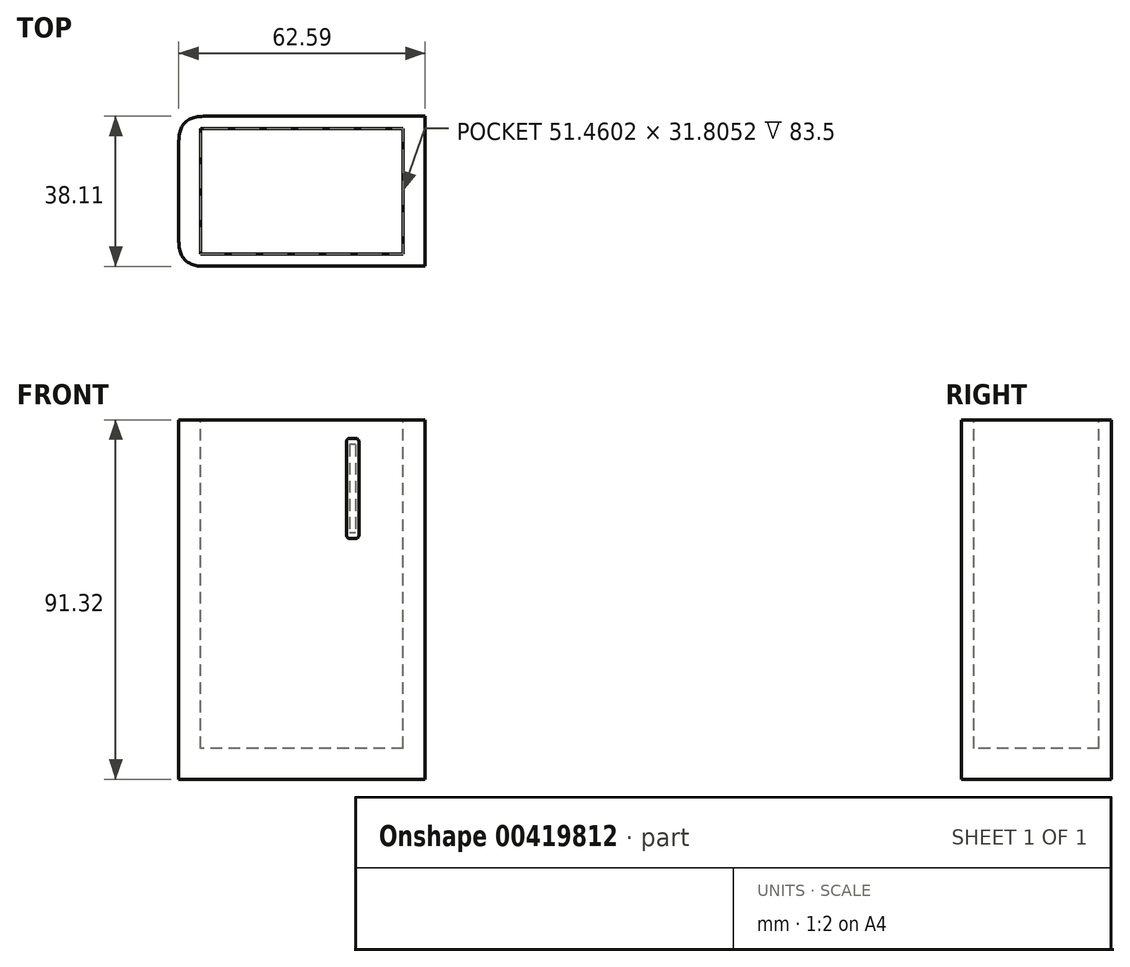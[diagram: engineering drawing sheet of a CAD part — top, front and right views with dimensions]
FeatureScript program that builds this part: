
annotation { "Feature Type Name" : "Feature", "Feature Type Description" : "" }
export const myFeature = defineFeature(function(context is Context, id is Id, definition is map)
    precondition{}
    {
        {
            var Q0;
            Q0=qCreatedBy(makeId("Front.planeOp"),FACE);
            var sketch = newSketch(context, id + "F0", { "sketchPlane" : qUnion([Q0])});
            skLineSegment(sketch, "E0", {"start": v(-32.63, 45.72) * mm, "end": v(-32.63, -30.6) * mm});
            skLineSegment(sketch, "E1", {"start": v(-32.63, -30.6) * mm, "end": v(49.96, -30.6) * mm});
            skLineSegment(sketch, "E2", {"start": v(49.96, -30.6) * mm, "end": v(49.96, 45.72) * mm});
            skLineSegment(sketch, "E3", {"start": v(49.96, 45.72) * mm, "end": v(-32.63, 45.72) * mm});
            skSolve(sketch);
        }
        {
            var Q0;
            Q0=makeQuery(id+"F0.imprint","IMPRINT",FACE,{"disambiguationData":[TD([[makeQuery(id+"F0.imprint","IMPRINT",EDGE,{"derivedFrom":sQuery(id+"F0.wireOp",EDGE,"E0")}),1.0]])]});
            extrude(context, id + "F1", {"entities" : qUnion([Q0]), "depth" : 25.4 * mm});
        }
        {
            var Q0;
            Q0=makeQuery(id+"F1.opExtrude","CAP_FACE",FACE,{"disambiguationData":[OSD([sQuery(id+"F0.wireOp",EDGE,"E0"),sQuery(id+"F0.wireOp",EDGE,"E1"),sQuery(id+"F0.wireOp",EDGE,"E2"),sQuery(id+"F0.wireOp",EDGE,"E3")])],"isStart":false});
            extrude(context, id + "F2", {"entities" : qUnion([Q0]), "operationType" : NewBodyOperationType.ADD, "depth" : 12.7 * mm});
        }
        {
            var Q0;
            {var subQ0=sQuery(id+"F0.wireOp",EDGE,"E3");Q0=makeQuery(id+"F2.boolean.opBoolean","MERGE",FACE,{"derivedFrom":[makeQuery(id+"F1.opExtrude","SWEPT_FACE",FACE,{"disambiguationData":[OSD([subQ0])]}),makeQuery(id+"F2.opExtrude","SWEPT_FACE",FACE,{"disambiguationData":[OSD([subQ0])]})]});}
            var sketch = newSketch(context, id + "F3", { "sketchPlane" : qUnion([Q0])});
            skLineSegment(sketch, "E4.bottom", {"start": v(44.4, -3.15) * mm, "end": v(-27.07, -3.15) * mm});
            skLineSegment(sketch, "E4.top", {"start": v(44.4, -34.95) * mm, "end": v(-27.07, -34.95) * mm});
            skLineSegment(sketch, "E4.left", {"start": v(44.4, -3.15) * mm, "end": v(44.4, -34.95) * mm});
            skLineSegment(sketch, "E4.right", {"start": v(-27.07, -3.15) * mm, "end": v(-27.07, -34.95) * mm});
            skPoint(sketch, "E4.middle", {"position": v(8.66, -19.05) * mm});
            skPoint(sketch, "E4.middle.positionSnap0", {"position": v(-32.63, -19.05) * mm});
            skPoint(sketch, "E4.middle.positionSnap1", {"position": v(8.66, 0) * mm});
            skPoint(sketch, "E4.centerSnap0", {"position": v(-32.63, -19.05) * mm});
            skPoint(sketch, "E4.centerSnap1", {"position": v(8.66, 0) * mm});
            skSolve(sketch);
        }
        {
            var Q0;
            Q0=makeQuery(id+"F3.imprint","IMPRINT",FACE,{"disambiguationData":[TD([[makeQuery(id+"F3.imprint","IMPRINT",EDGE,{"derivedFrom":sQuery(id+"F3.wireOp",EDGE,"E4.bottom")}),1.0]])]});
            extrude(context, id + "F4", {"entities" : qUnion([Q0]), "operationType" : NewBodyOperationType.REMOVE, "oppositeDirection" : true, "depth" : 63.5 * mm});
        }
        {
            var Q0;
            Q0=makeQuery(id+"F2.opExtrude","CAP_FACE",FACE,{"disambiguationData":[OSD([sQuery(id+"F0.wireOp",EDGE,"E0"),sQuery(id+"F0.wireOp",EDGE,"E1"),sQuery(id+"F0.wireOp",EDGE,"E2"),sQuery(id+"F0.wireOp",EDGE,"E3")])],"isStart":false});
            var sketch = newSketch(context, id + "F5", { "sketchPlane" : qUnion([Q0])});
            skLineSegment(sketch, "E5", {"start": v(49.96, 45.72) * mm, "end": v(12.33, 45.72) * mm});
            skLineSegment(sketch, "E6", {"start": v(49.96, 45.72) * mm, "end": v(49.96, 39.4) * mm});
            skLineSegment(sketch, "E7", {"start": v(12.33, 39.4) * mm, "end": v(10.8, 39.4) * mm});
            skLineSegment(sketch, "E8", {"start": v(10.8, 39.4) * mm, "end": v(10.8, 17.15) * mm});
            skLineSegment(sketch, "E9", {"start": v(10.8, 17.15) * mm, "end": v(12.33, 17.15) * mm});
            skLineSegment(sketch, "E10", {"start": v(12.33, 39.4) * mm, "end": v(12.33, 17.15) * mm});
            skSolve(sketch);
        }
        {
            var Q0;
            Q0=makeQuery(id+"F5.imprint","IMPRINT",FACE,{"disambiguationData":[TD([[makeQuery(id+"F5.imprint","IMPRINT",EDGE,{"derivedFrom":sQuery(id+"F5.wireOp",EDGE,"E7")}),1.0]])]});
            extrude(context, id + "F6", {"entities" : qUnion([Q0]), "operationType" : NewBodyOperationType.ADD, "depth" : 1 / 203.2 * mm});
        }
        {
            var Q0;
            Q0=makeQuery(id+"F6.opExtrude","CAP_FACE",FACE,{"disambiguationData":[OSD([sQuery(id+"F5.wireOp",EDGE,"E7"),sQuery(id+"F5.wireOp",EDGE,"E8"),sQuery(id+"F5.wireOp",EDGE,"E9"),sQuery(id+"F5.wireOp",EDGE,"E10")])],"isStart":false});
            var sketch = newSketch(context, id + "F7", { "sketchPlane" : qUnion([Q0])});
            skLineSegment(sketch, "E11", {"start": v(10.02, 39.4) * mm, "end": v(10.02, 41) * mm});
            skPoint(sketch, "E12.endSnap0", {"position": v(11.56, 39.4) * mm});
            skLineSegment(sketch, "E13.MirrorCS", {"start": v(13.1, 39.4) * mm, "end": v(13.1, 41) * mm});
            skPoint(sketch, "E14.endSnap0", {"position": v(12.33, 28.27) * mm});
            skLineSegment(sketch, "E15.MirrorCS", {"start": v(13.1, 17.15) * mm, "end": v(13.1, 15.55) * mm});
            skLineSegment(sketch, "E16.MirrorCS", {"start": v(10.02, 17.15) * mm, "end": v(10.02, 15.55) * mm});
            skLineSegment(sketch, "E17", {"start": v(10.02, 41) * mm, "end": v(13.1, 41) * mm});
            skLineSegment(sketch, "E18", {"start": v(10.02, 15.55) * mm, "end": v(13.1, 15.55) * mm});
            skLineSegment(sketch, "E19", {"start": v(13.1, 17.15) * mm, "end": v(13.1, 39.4) * mm});
            skLineSegment(sketch, "E20", {"start": v(10.02, 39.4) * mm, "end": v(10.02, 17.15) * mm});
            skSolve(sketch);
        }
        {
            var Q0;
            Q0=qSketchRegion(id+"F7",true);
            extrude(context, id + "F8", {"entities" : qUnion([Q0]), "depth" : 1 / 406.4 * mm});
        }
        {
            var Q0;
            Q0=makeQuery(id+"F8.opExtrude","SWEPT_EDGE",EDGE,{"disambiguationData":[OSD([sQuery(id+"F7.wireOp",EDGE,"E13.MirrorCS"),sQuery(id+"F7.wireOp",EDGE,"E17")])]});
            var Q1;
            Q1=makeQuery(id+"F8.opExtrude","SWEPT_EDGE",EDGE,{"disambiguationData":[OSD([sQuery(id+"F7.wireOp",EDGE,"E11"),sQuery(id+"F7.wireOp",EDGE,"E17")])]});
            var Q2;
            Q2=makeQuery(id+"F8.opExtrude","SWEPT_EDGE",EDGE,{"disambiguationData":[OSD([sQuery(id+"F7.wireOp",EDGE,"E15.MirrorCS"),sQuery(id+"F7.wireOp",EDGE,"E18")])]});
            var Q3;
            Q3=makeQuery(id+"F8.opExtrude","SWEPT_EDGE",EDGE,{"disambiguationData":[OSD([sQuery(id+"F7.wireOp",EDGE,"E16.MirrorCS"),sQuery(id+"F7.wireOp",EDGE,"E18")])]});
            fillet(context, id + "F9", {"entities" : qUnion([Q0, Q1, Q2, Q3]), "radius" : 0.76 * mm, "tangentPropagation" : true, "allowEdgeOverflow" : false});
        }
        {
            var Q0;
            Q0=makeQuery(id+"F4.boolean.opBoolean","COPY",FACE,{"derivedFrom":makeQuery(id+"F4.opExtrude","SWEPT_FACE",FACE,{"disambiguationData":[OSD([sQuery(id+"F3.wireOp",EDGE,"E4.left")])]})});
            extrude(context, id + "F10", {"entities" : qUnion([Q0]), "operationType" : NewBodyOperationType.ADD, "depth" : 20 * mm});
        }
        {
            var Q0;
            {var subQ0=sQuery(id+"F0.wireOp",EDGE,"E2");Q0=makeQuery(id+"F2.boolean.opBoolean","MERGE",FACE,{"derivedFrom":[makeQuery(id+"F1.opExtrude","SWEPT_FACE",FACE,{"disambiguationData":[OSD([subQ0])]}),makeQuery(id+"F2.opExtrude","SWEPT_FACE",FACE,{"disambiguationData":[OSD([subQ0])]})]});}
            extrude(context, id + "F11", {"entities" : qUnion([Q0]), "operationType" : NewBodyOperationType.REMOVE, "oppositeDirection" : true, "depth" : 20 * mm});
        }
        {
            var Q0;
            {var subQ0=sQuery(id+"F0.wireOp",EDGE,"E2");Q0=makeQuery(id+"F11.boolean.opBoolean","COPY",EDGE,{"derivedFrom":makeQuery(id+"F11.opExtrude","CAP_EDGE",EDGE,{"disambiguationData":[OSD([subQ0]),TDD([makeQuery(id+"F1.opExtrude","CAP_EDGE",EDGE,{"disambiguationData":[OSD([subQ0])],"isStart":true})])],"isStart":false})});}
            var Q1;
            {var subQ0=sQuery(id+"F0.wireOp",EDGE,"E2");Q1=makeQuery(id+"F11.boolean.opBoolean","COPY",EDGE,{"derivedFrom":makeQuery(id+"F11.opExtrude","CAP_EDGE",EDGE,{"disambiguationData":[OSD([subQ0]),TDD([makeQuery(id+"F2.opExtrude","CAP_EDGE",EDGE,{"disambiguationData":[OSD([subQ0])],"isStart":false})])],"isStart":false})});}
            var Q2;
            Q2=makeQuery(id+"F1.opExtrude","CAP_EDGE",EDGE,{"disambiguationData":[OSD([sQuery(id+"F0.wireOp",EDGE,"E0")])],"isStart":true});
            var Q3;
            Q3=makeQuery(id+"F2.opExtrude","CAP_EDGE",EDGE,{"disambiguationData":[OSD([sQuery(id+"F0.wireOp",EDGE,"E0")])],"isStart":false});
            fillet(context, id + "F12", {"entities" : qUnion([Q0, Q1, Q2, Q3]), "radius" : 6.35 * mm, "rho" : 0.5, "crossSection" : FilletCrossSection.CONIC, "allowEdgeOverflow" : false});
        }
        {
            var Q0;
            {var subQ0=sQuery(id+"F0.wireOp",EDGE,"E1");Q0=makeQuery(id+"F2.boolean.opBoolean","MERGE",FACE,{"derivedFrom":[makeQuery(id+"F1.opExtrude","SWEPT_FACE",FACE,{"disambiguationData":[OSD([subQ0])]}),makeQuery(id+"F2.opExtrude","SWEPT_FACE",FACE,{"disambiguationData":[OSD([subQ0])]})]});}
            extrude(context, id + "F13", {"entities" : qUnion([Q0]), "operationType" : NewBodyOperationType.ADD, "depth" : 20 * mm});
        }
        {
            var Q0;
            Q0=makeQuery(id+"F4.boolean.opBoolean","COPY",FACE,{"derivedFrom":makeQuery(id+"F4.opExtrude","CAP_FACE",FACE,{"disambiguationData":[OSD([sQuery(id+"F3.wireOp",EDGE,"E4.bottom"),sQuery(id+"F3.wireOp",EDGE,"E4.top"),sQuery(id+"F3.wireOp",EDGE,"E4.left"),sQuery(id+"F3.wireOp",EDGE,"E4.right")])],"isStart":false})});
            extrude(context, id + "F14", {"entities" : qUnion([Q0]), "operationType" : NewBodyOperationType.REMOVE, "oppositeDirection" : true, "depth" : 20 * mm});
        }
        {
            var Q0;
            Q0=makeQuery(id+"F13.opExtrude","CAP_FACE",FACE,{"disambiguationData":[OSD([sQuery(id+"F0.wireOp",EDGE,"E1")])],"isStart":false});
            extrude(context, id + "F15", {"entities" : qUnion([Q0]), "operationType" : NewBodyOperationType.REMOVE, "oppositeDirection" : true, "depth" : 5 * mm});
        }
    });
